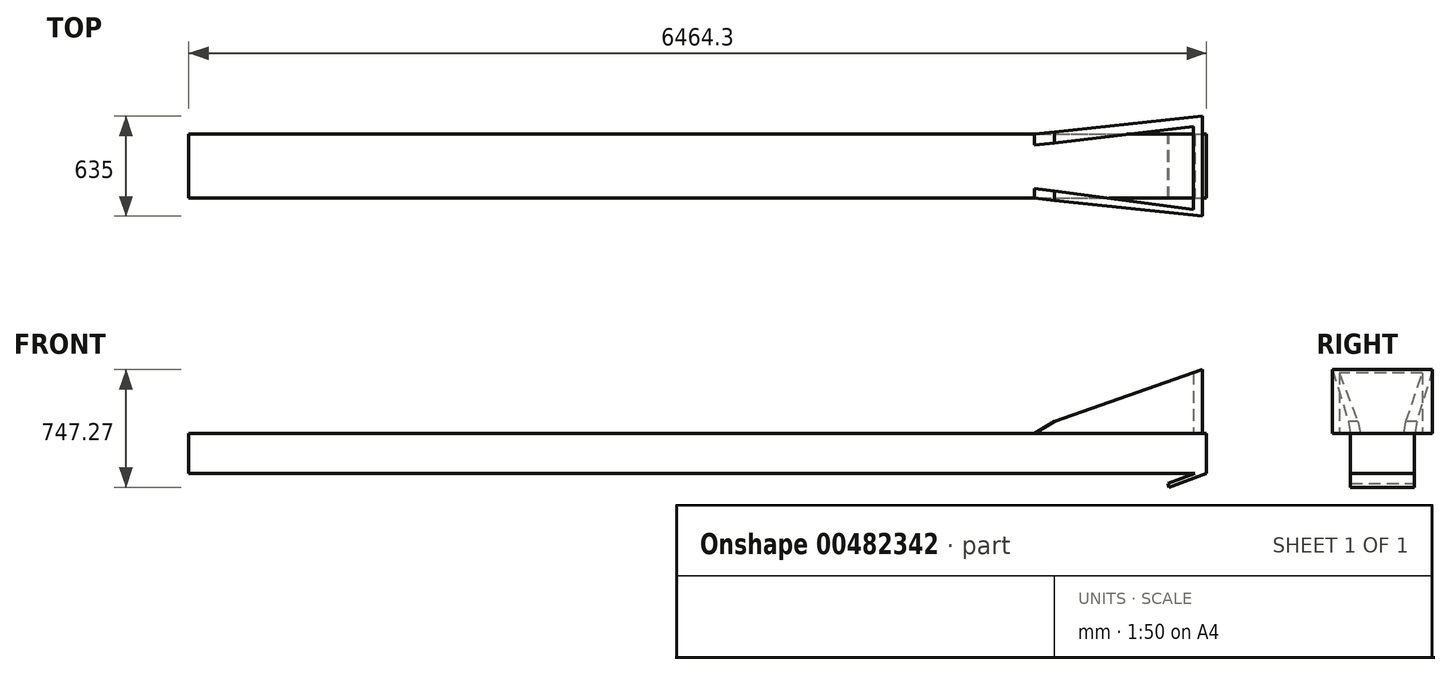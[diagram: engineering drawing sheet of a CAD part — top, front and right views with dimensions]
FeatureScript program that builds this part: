
annotation { "Feature Type Name" : "Feature", "Feature Type Description" : "" }
export const myFeature = defineFeature(function(context is Context, id is Id, definition is map)
    precondition{}
    {
        {
            var Q0;
            Q0=qCreatedBy(makeId("Top.planeOp"),FACE);
            var sketch = newSketch(context, id + "F0", { "sketchPlane" : qUnion([Q0])});
            skLineSegment(sketch, "E0.bottom", {"start": v(0, 0) * mm, "end": v(6464.3, 0) * mm});
            skLineSegment(sketch, "E0.top", {"start": v(0, 406.4) * mm, "end": v(6464.3, 406.4) * mm});
            skLineSegment(sketch, "E0.left", {"start": v(0, 0) * mm, "end": v(0, 406.4) * mm});
            skLineSegment(sketch, "E0.right", {"start": v(6464.3, 0) * mm, "end": v(6464.3, 406.4) * mm});
            skSolve(sketch);
        }
        {
            var Q0;
            Q0 = qSketchRegion(id + "F0", true);
            extrude(context, id + "F1", {"entities" : qUnion([Q0]), "depth" : 254 * mm, "offsetDistance" : 25.4 * mm});
        }
        {
            var Q0;
            Q0=makeQuery(id+"F1.opExtrude","SWEPT_FACE",FACE,{"disambiguationData":[OSD([sQuery(id+"F0.wireOp",EDGE,"E0.bottom")])]});
            cPlane(context, id + "F2", {"entities" : qUnion([Q0]), "cplaneType" : CPlaneType.OFFSET, "offset" : 114.3 * mm, "width" : 152.4 * mm, "height" : 152.4 * mm});
        }
        {
            var Q0;
            Q0=qCreatedBy(id+"F2.planeOp",FACE);
            var sketch = newSketch(context, id + "F3", { "sketchPlane" : qUnion([Q0])});
            skLineSegment(sketch, "E1", {"start": v(6438.9, 660.4) * mm, "end": v(5499.1, 330.2) * mm});
            skLineSegment(sketch, "E2", {"start": v(5499.1, 330.2) * mm, "end": v(5372.1, 254) * mm});
            skLineSegment(sketch, "E3", {"start": v(5372.1, 254) * mm, "end": v(6438.9, 254) * mm});
            skLineSegment(sketch, "E4", {"start": v(6438.9, 254) * mm, "end": v(6438.9, 660.4) * mm});
            skSolve(sketch);
        }
        {
            var Q0;
            Q0 = qSketchRegion(id + "F3", true);
            extrude(context, id + "F4", {"entities" : qUnion([Q0]), "operationType" : NewBodyOperationType.ADD, "oppositeDirection" : true, "depth" : 635 * mm, "offsetDistance" : 25.4 * mm});
        }
        {
            var Q0;
            {var subQ0=sQuery(id+"F0.wireOp",EDGE,"E0.left");var subQ1=sQuery(id+"F0.wireOp",EDGE,"E0.top");var subQ2=sQuery(id+"F0.wireOp",EDGE,"E0.bottom");Q0=makeQuery(id+"F4.boolean.opBoolean","SPLIT",FACE,{"disambiguationData":[TD([makeQuery(id+"F1.opExtrude","SWEPT_FACE",FACE,{"disambiguationData":[OSD([subQ0])]})])],"derivedFrom":makeQuery(id+"F1.opExtrude","CAP_FACE",FACE,{"disambiguationData":[OSD([subQ2,subQ1,subQ0,sQuery(id+"F0.wireOp",EDGE,"E0.right")])],"isStart":false})});}
            var sketch = newSketch(context, id + "F5", { "sketchPlane" : qUnion([Q0])});
            skLineSegment(sketch, "E5", {"start": v(5372.1, 406.4) * mm, "end": v(6438.9, 520.7) * mm});
            skLineSegment(sketch, "E6", {"start": v(6438.9, 520.7) * mm, "end": v(5372.1, 520.7) * mm});
            skLineSegment(sketch, "E7", {"start": v(5372.1, 520.7) * mm, "end": v(5372.1, 406.4) * mm});
            skLineSegment(sketch, "E8", {"start": v(5372.1, 0) * mm, "end": v(6438.9, -114.3) * mm});
            skLineSegment(sketch, "E9", {"start": v(6438.9, -114.3) * mm, "end": v(5372.1, -114.3) * mm});
            skLineSegment(sketch, "E10", {"start": v(5372.1, -114.3) * mm, "end": v(5372.1, 0) * mm});
            skSolve(sketch);
        }
        {
            var Q0;
            Q0 = qSketchRegion(id + "F5", true);
            extrude(context, id + "F6", {"entities" : qUnion([Q0]), "operationType" : NewBodyOperationType.REMOVE, "endBound" : BoundingType.THROUGH_ALL, "depth" : 25.4 * mm, "offsetDistance" : 25.4 * mm});
        }
        {
            var Q0;
            {var subQ0=sQuery(id+"F0.wireOp",EDGE,"E0.left");var subQ1=sQuery(id+"F0.wireOp",EDGE,"E0.top");var subQ2=sQuery(id+"F0.wireOp",EDGE,"E0.bottom");Q0=makeQuery(id+"F4.boolean.opBoolean","SPLIT",FACE,{"disambiguationData":[TD([makeQuery(id+"F1.opExtrude","SWEPT_FACE",FACE,{"disambiguationData":[OSD([subQ0])]})])],"derivedFrom":makeQuery(id+"F1.opExtrude","CAP_FACE",FACE,{"disambiguationData":[OSD([subQ2,subQ1,subQ0,sQuery(id+"F0.wireOp",EDGE,"E0.right")])],"isStart":false})});}
            var sketch = newSketch(context, id + "F7", { "sketchPlane" : qUnion([Q0])});
            skLineSegment(sketch, "E11", {"start": v(5333.49, 332.14) * mm, "end": v(5333.49, 68.01) * mm});
            skLineSegment(sketch, "E12", {"start": v(5333.49, 68.01) * mm, "end": v(6380.66, -71.82) * mm});
            skLineSegment(sketch, "E13", {"start": v(6380.66, -71.82) * mm, "end": v(6380.66, 456.43) * mm});
            skLineSegment(sketch, "E14", {"start": v(6380.66, 456.43) * mm, "end": v(5333.49, 332.14) * mm});
            skSolve(sketch);
        }
        {
            var Q0;
            Q0 = qSketchRegion(id + "F7", true);
            extrude(context, id + "F8", {"entities" : qUnion([Q0]), "operationType" : NewBodyOperationType.REMOVE, "endBound" : BoundingType.THROUGH_ALL, "depth" : 25.4 * mm, "offsetDistance" : 25.4 * mm});
        }
        {
            var Q0;
            Q0=makeQuery(id+"F1.opExtrude","CAP_FACE",FACE,{"disambiguationData":[OSD([sQuery(id+"F0.wireOp",EDGE,"E0.bottom"),sQuery(id+"F0.wireOp",EDGE,"E0.top"),sQuery(id+"F0.wireOp",EDGE,"E0.left"),sQuery(id+"F0.wireOp",EDGE,"E0.right")])],"isStart":true});
            var Q1;
            Q1=makeQuery(id+"F1.opExtrude","CAP_EDGE",EDGE,{"disambiguationData":[OSD([sQuery(id+"F0.wireOp",EDGE,"E0.right")])],"isStart":true});
            cPlane(context, id + "F9", {"entities" : qUnion([Q0, Q1]), "cplaneType" : CPlaneType.LINE_ANGLE, "offset" : 25.4 * mm, "angle" : 20 * degree, "oppositeDirection" : true, "width" : 152.4 * mm, "height" : 152.4 * mm});
        }
        {
            var Q0;
            Q0=qCreatedBy(id+"F9.planeOp",FACE);
            var sketch = newSketch(context, id + "F10", { "sketchPlane" : qUnion([Q0])});
            skLineSegment(sketch, "E15.bottom", {"start": v(6074.46, 0) * mm, "end": v(5820.46, 0) * mm});
            skLineSegment(sketch, "E15.top", {"start": v(6074.46, 406.4) * mm, "end": v(5820.46, 406.4) * mm});
            skLineSegment(sketch, "E15.left", {"start": v(6074.46, 0) * mm, "end": v(6074.46, 406.4) * mm});
            skLineSegment(sketch, "E15.right", {"start": v(5820.46, 0) * mm, "end": v(5820.46, 406.4) * mm});
            skSolve(sketch);
        }
        {
            var Q0;
            Q0 = qSketchRegion(id + "F10", true);
            extrude(context, id + "F11", {"entities" : qUnion([Q0]), "operationType" : NewBodyOperationType.ADD, "depth" : 25.4 * mm, "offsetDistance" : 25.4 * mm});
        }
    });
